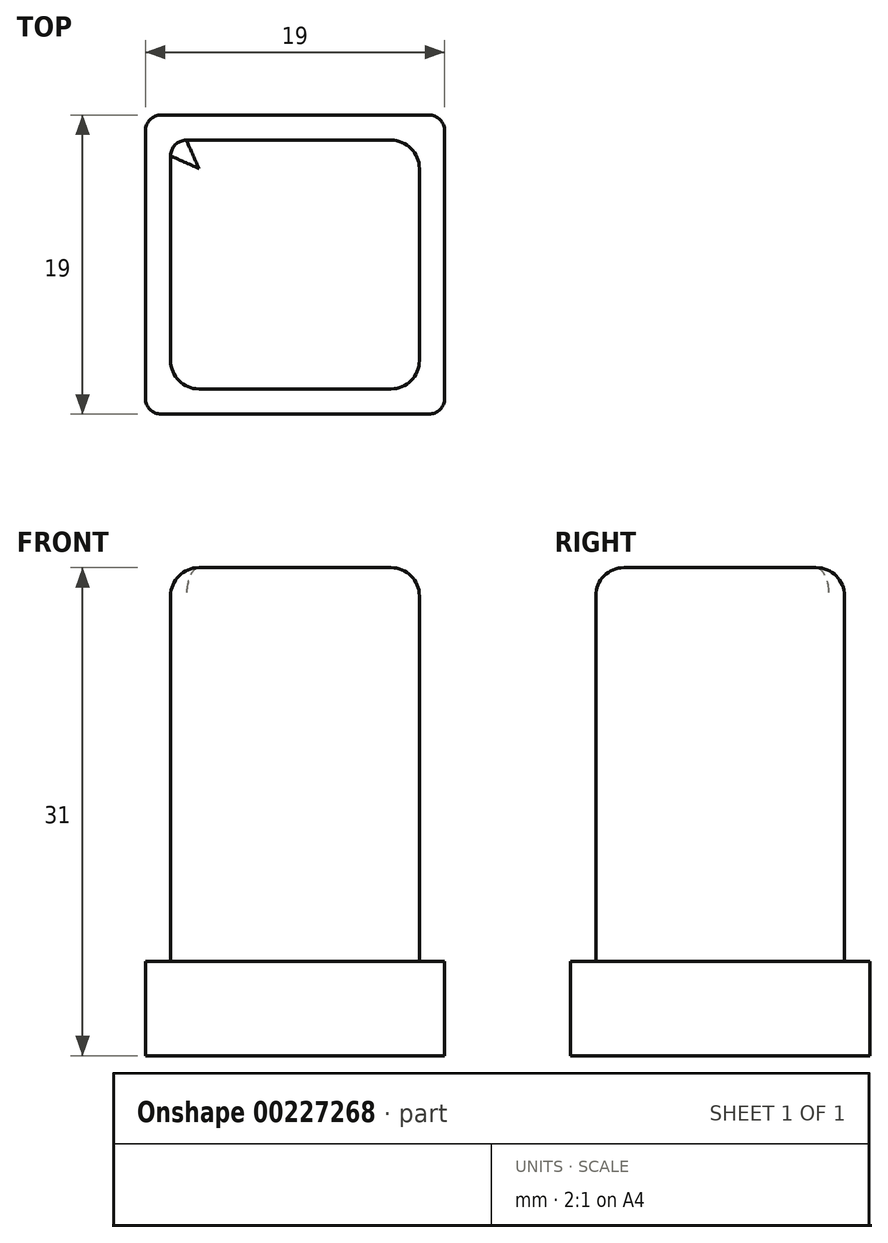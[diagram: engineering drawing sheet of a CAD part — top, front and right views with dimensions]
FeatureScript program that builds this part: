
annotation { "Feature Type Name" : "Feature", "Feature Type Description" : "" }
export const myFeature = defineFeature(function(context is Context, id is Id, definition is map)
    precondition{}
    {
        {
            var Q0;
            Q0=qCreatedBy(makeId("Top.planeOp"),FACE);
            var sketch = newSketch(context, id + "F0", { "sketchPlane" : qUnion([Q0])});
            skLineSegment(sketch, "E0.bottom", {"start": v(0, 0) * mm, "end": v(19, 0) * mm});
            skLineSegment(sketch, "E0.top", {"start": v(0, -19) * mm, "end": v(19, -19) * mm});
            skLineSegment(sketch, "E0.left", {"start": v(0, 0) * mm, "end": v(0, -19) * mm});
            skLineSegment(sketch, "E0.right", {"start": v(19, 0) * mm, "end": v(19, -19) * mm});
            skSolve(sketch);
        }
        {
            var Q0;
            Q0=makeQuery(id+"F0.imprint","IMPRINT",FACE,{"disambiguationData":[TD([[makeQuery(id+"F0.imprint","IMPRINT",EDGE,{"derivedFrom":sQuery(id+"F0.wireOp",EDGE,"E0.bottom")}),-1.0]])]});
            extrude(context, id + "F1", {"entities" : qUnion([Q0]), "depth" : 6 * mm});
        }
        {
            var Q0;
            Q0=makeQuery(id+"F1.opExtrude","CAP_FACE",FACE,{"disambiguationData":[OSD([sQuery(id+"F0.wireOp",EDGE,"E0.bottom"),sQuery(id+"F0.wireOp",EDGE,"E0.top"),sQuery(id+"F0.wireOp",EDGE,"E0.left"),sQuery(id+"F0.wireOp",EDGE,"E0.right")])],"isStart":false});
            var sketch = newSketch(context, id + "F2", { "sketchPlane" : qUnion([Q0])});
            skLineSegment(sketch, "E1.bottom", {"start": v(1.6, -1.6) * mm, "end": v(17.4, -1.6) * mm});
            skLineSegment(sketch, "E1.top", {"start": v(1.6, -17.4) * mm, "end": v(17.4, -17.4) * mm});
            skLineSegment(sketch, "E1.left", {"start": v(1.6, -1.6) * mm, "end": v(1.6, -17.4) * mm});
            skLineSegment(sketch, "E1.right", {"start": v(17.4, -1.6) * mm, "end": v(17.4, -17.4) * mm});
            skSolve(sketch);
        }
        {
            var Q0;
            Q0 = qSketchRegion(id + "F2", true);
            extrude(context, id + "F3", {"entities" : qUnion([Q0]), "operationType" : NewBodyOperationType.ADD, "depth" : 25 * mm});
        }
        {
            var Q0;
            Q0=makeQuery(id+"F3.opExtrude","SWEPT_EDGE",EDGE,{"disambiguationData":[OSD([sQuery(id+"F2.wireOp",EDGE,"E1.top"),sQuery(id+"F2.wireOp",EDGE,"E1.right")])]});
            fillet(context, id + "F4", {"entities" : qUnion([Q0]), "radius" : 1.8 * mm, "tangentPropagation" : true, "allowEdgeOverflow" : false});
        }
        {
            var Q0;
            Q0=makeQuery(id+"F3.opExtrude","SWEPT_EDGE",EDGE,{"disambiguationData":[OSD([sQuery(id+"F2.wireOp",EDGE,"E1.bottom"),sQuery(id+"F2.wireOp",EDGE,"E1.right")])]});
            fillet(context, id + "F5", {"entities" : qUnion([Q0]), "radius" : 1.8 * mm, "tangentPropagation" : true, "allowEdgeOverflow" : false});
        }
        {
            var Q0;
            Q0=makeQuery(id+"F3.opExtrude","SWEPT_EDGE",EDGE,{"disambiguationData":[OSD([sQuery(id+"F2.wireOp",EDGE,"E1.top"),sQuery(id+"F2.wireOp",EDGE,"E1.left")])]});
            fillet(context, id + "F6", {"entities" : qUnion([Q0]), "radius" : 1.8 * mm, "tangentPropagation" : true, "allowEdgeOverflow" : false});
        }
        {
            var Q0;
            Q0=makeQuery(id+"F3.opExtrude","SWEPT_EDGE",EDGE,{"disambiguationData":[OSD([sQuery(id+"F2.wireOp",EDGE,"E1.bottom"),sQuery(id+"F2.wireOp",EDGE,"E1.left")])]});
            fillet(context, id + "F7", {"entities" : qUnion([Q0]), "radius" : 1 * mm, "tangentPropagation" : true, "allowEdgeOverflow" : false});
        }
        {
            var Q0;
            Q0=makeQuery(id+"F1.opExtrude","SWEPT_EDGE",EDGE,{"disambiguationData":[OSD([sQuery(id+"F0.wireOp",EDGE,"E0.top"),sQuery(id+"F0.wireOp",EDGE,"E0.right")])]});
            fillet(context, id + "F8", {"entities" : qUnion([Q0]), "radius" : 1 * mm, "tangentPropagation" : true, "allowEdgeOverflow" : false});
        }
        {
            var Q0;
            Q0=makeQuery(id+"F1.opExtrude","SWEPT_EDGE",EDGE,{"disambiguationData":[OSD([sQuery(id+"F0.wireOp",EDGE,"E0.top"),sQuery(id+"F0.wireOp",EDGE,"E0.left")])]});
            fillet(context, id + "F9", {"entities" : qUnion([Q0]), "radius" : 1 * mm, "tangentPropagation" : true, "allowEdgeOverflow" : false});
        }
        {
            var Q0;
            Q0=makeQuery(id+"F1.opExtrude","SWEPT_EDGE",EDGE,{"disambiguationData":[OSD([sQuery(id+"F0.wireOp",EDGE,"E0.bottom"),sQuery(id+"F0.wireOp",EDGE,"E0.right")])]});
            fillet(context, id + "F10", {"entities" : qUnion([Q0]), "radius" : 1 * mm, "tangentPropagation" : true, "allowEdgeOverflow" : false});
        }
        {
            var Q0;
            Q0=makeQuery(id+"F1.opExtrude","SWEPT_EDGE",EDGE,{"disambiguationData":[OSD([sQuery(id+"F0.wireOp",EDGE,"E0.bottom"),sQuery(id+"F0.wireOp",EDGE,"E0.left")])]});
            fillet(context, id + "F11", {"entities" : qUnion([Q0]), "radius" : 1 * mm, "tangentPropagation" : true, "allowEdgeOverflow" : false});
        }
        {
            var Q0;
            {var subQ0=sQuery(id+"F2.wireOp",EDGE,"E1.left");var subQ1=sQuery(id+"F2.wireOp",EDGE,"E1.bottom");Q0=makeQuery(id+"F7.opFillet","BLEND_EDGE",EDGE,{"blendedFrom":[makeQuery(id+"F3.opExtrude","SWEPT_EDGE",EDGE,{"disambiguationData":[OSD([subQ1,subQ0])]}),makeQuery(id+"F3.opExtrude","CAP_FACE",FACE,{"disambiguationData":[OSD([subQ1,sQuery(id+"F2.wireOp",EDGE,"E1.top"),subQ0,sQuery(id+"F2.wireOp",EDGE,"E1.right")])],"isStart":false})],"blendedInto":[makeQuery(id+"F3.opExtrude","CAP_FACE",FACE,{"disambiguationData":[OSD([subQ1,sQuery(id+"F2.wireOp",EDGE,"E1.top"),subQ0,sQuery(id+"F2.wireOp",EDGE,"E1.right")])],"isStart":false})]});}
            fillet(context, id + "F12", {"entities" : qUnion([Q0]), "radius" : 1.8 * mm, "tangentPropagation" : true, "allowEdgeOverflow" : false});
        }
    });
